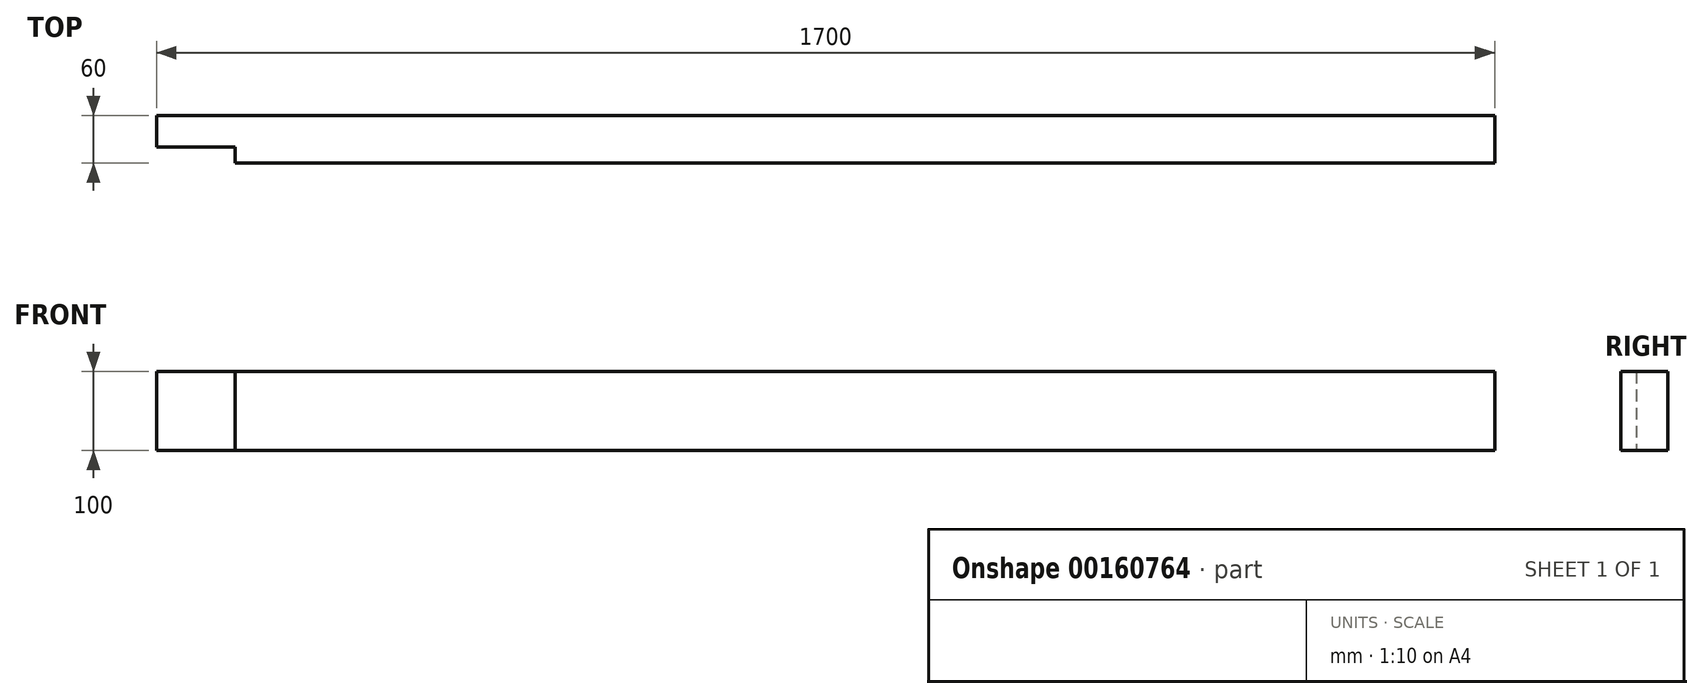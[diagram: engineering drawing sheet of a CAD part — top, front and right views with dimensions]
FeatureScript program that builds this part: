
annotation { "Feature Type Name" : "Feature", "Feature Type Description" : "" }
export const myFeature = defineFeature(function(context is Context, id is Id, definition is map)
    precondition{}
    {
        {
            assignVariable(context, id + "F0", {"name" : "L", "anyValue" : 1800 * mm - 200 * mm});
        }
        {
            var Q0;
            Q0=qCreatedBy(makeId("Right.planeOp"),FACE);
            var sketch = newSketch(context, id + "F1", { "sketchPlane" : qUnion([Q0])});
            skLineSegment(sketch, "E0.bottom", {"start": v(-30, 50) * mm, "end": v(30, 50) * mm});
            skLineSegment(sketch, "E0.top", {"start": v(-30, -50) * mm, "end": v(30, -50) * mm});
            skLineSegment(sketch, "E0.left", {"start": v(-30, 50) * mm, "end": v(-30, -50) * mm});
            skLineSegment(sketch, "E0.right", {"start": v(30, 50) * mm, "end": v(30, -50) * mm});
            skPoint(sketch, "E0.middle", {"position": v(0, 0) * mm});
            skSolve(sketch);
        }
        {
            var Q0;
            Q0 = qSketchRegion(id + "F1", true);
            extrude(context, id + "F2", {"entities" : qUnion([Q0]), "endBound" : BoundingType.SYMMETRIC, "depth" : getVariable(context, 'L')});
        }
        {
            var Q0;
            Q0=makeQuery(id+"F2.opExtrude","CAP_FACE",FACE,{"disambiguationData":[OSD([sQuery(id+"F1.wireOp",EDGE,"E0.bottom"),sQuery(id+"F1.wireOp",EDGE,"E0.top"),sQuery(id+"F1.wireOp",EDGE,"E0.left"),sQuery(id+"F1.wireOp",EDGE,"E0.right")])],"isStart":true});
            var sketch = newSketch(context, id + "F3", { "sketchPlane" : qUnion([Q0])});
            skLineSegment(sketch, "E1.bottom", {"start": v(-30, 50) * mm, "end": v(10, 50) * mm});
            skLineSegment(sketch, "E1.top", {"start": v(-30, -50) * mm, "end": v(10, -50) * mm});
            skLineSegment(sketch, "E1.left", {"start": v(-30, 50) * mm, "end": v(-30, -50) * mm});
            skLineSegment(sketch, "E1.right", {"start": v(10, 50) * mm, "end": v(10, -50) * mm});
            skSolve(sketch);
        }
        {
            var Q0;
            Q0 = qSketchRegion(id + "F3", true);
            extrude(context, id + "F4", {"entities" : qUnion([Q0]), "operationType" : NewBodyOperationType.ADD, "depth" : 100 * mm});
        }
    });
